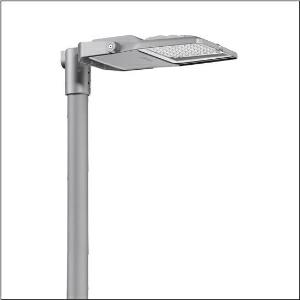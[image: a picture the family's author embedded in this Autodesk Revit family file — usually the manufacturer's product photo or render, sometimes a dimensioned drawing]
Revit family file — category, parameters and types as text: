
# Revit family: floodlight_fl_21_iq_mini___pl61_5xa7772c2c3a_f769
name_source: partatom
category: Lighting Fixtures
units: mm (PartAtom-declared; Revit-internal decimal feet)

## family parameters
Cut with Voids When Loaded = No
Host = Face
Light Source = No
Part Type = Normal
Room Calculation Point = No
Round Connector Dimension = Use Diameter
Shared = No

## types (1)
- --- (1 x LED, 11980 lm, 87.2 W, 3000K)
    Apparent Load = 87 VA
    CIE Flux Codes = 33 65 98 100 100
    Color Rendering = 70
    Color Temperature = 3000K
    Default Elevation = 1800 mm
    Description = Floodlight FL 21 iQ mini, floodlight, primary light control with lens, of PMMA, primary optical cover: protective disc, of toughened safety glass, transparent, light distribution: PL61, light emission: direct distribution, installation type: surface-mounted, LED, High Power LED, rated luminous flux: 11.980lm, luminous efficacy: 137lm/W, light colour: 730, colour temperature: 3000K, control: Auto-Match, Temp-Guard, Night-Set, Smart-Wire, Desk-Remote (wireless, voltage-free reading and setting of iQ features in the workshop via application-optimized NFC function/RFID function), optimised constant luminous flux control (CLO 2.0), Light-Fading, Lumen-Switch, with terminal, 6-pole, mains connection: 220..240V, AC, 50/60Hz, start of lifetime: 87W, end of service life: 92W, reduction: 40W, luminaire housing, of diecast aluminium, powder-coated, Siteco® metallic grey (DB 702S), corrosivity category C5 mid according to DIN EN ISO 12944, sealing non-destructively replaceable, please order mast flange separately, mast bracket, of steel, galvanised, powder-coated, protection rating (complete): IP66, insulation class (complete): insulation class II (safety insulation), certification: CE, ENEC, VDE, protection symbol: D, impact resistance: IK08, permissible operating ambient temperature: -40..+40°C, permissible operating ambient temperature for outdoor applications: -40..+50°C, standard: DIN EN 12944, LABS conformity tested according to VDMA 24364:2018-05, packaging unit: 1 piece

Light Distribution: PL61
    Height = 70 mm
    Lamp = 1 x LED
    Lamp Light Flux = 11980 lm
    Lamp Power = 87.2 W
    Lamp count = 1
    Length = 485 mm
    Luminous efficacy = 137 lm/W
    Manufacturer = Siteco
    ModVariant = No
    Model = 5XA7772C2C3A
    Number of Poles = 1
    OnlyDefault = Yes
    Power Factor = 1
    Product Name = Floodlight FL 21 iQ mini | PL61
    Product group = floodlight | pylon annexe
    ProductGroupID = 6200
    Protection Class = Protection class II
    Protection Degree = IP 66
    RLX_Detail_Level = 1
    RLX_Emergency_Light_Flux = 0 lm
    RLX_Emergency_Type = 0
    RLX_Emergency_Type_DB = No
    RlxData = <blob elided: 101349 chars, md5=114b2009>
    Socket = socket
    Standby Power = 0 W
    System Light Flux = 11980 lm
    System Power = 87 W
    Type Comments = factory setting: luminous flux: 100 % | dim-lin: 254 | 456 mA
    Type Image = l_1007125.jpg
    URL = http://relux.com
    VarID = @adj_144153
    Voltage = 0 V
    Weight = 0.00 kg
    Width = 337 mm

## geometry (parser evidence)
native form markers: Blend x4, Sweep x11
no freeform markers — native parametric forms only
